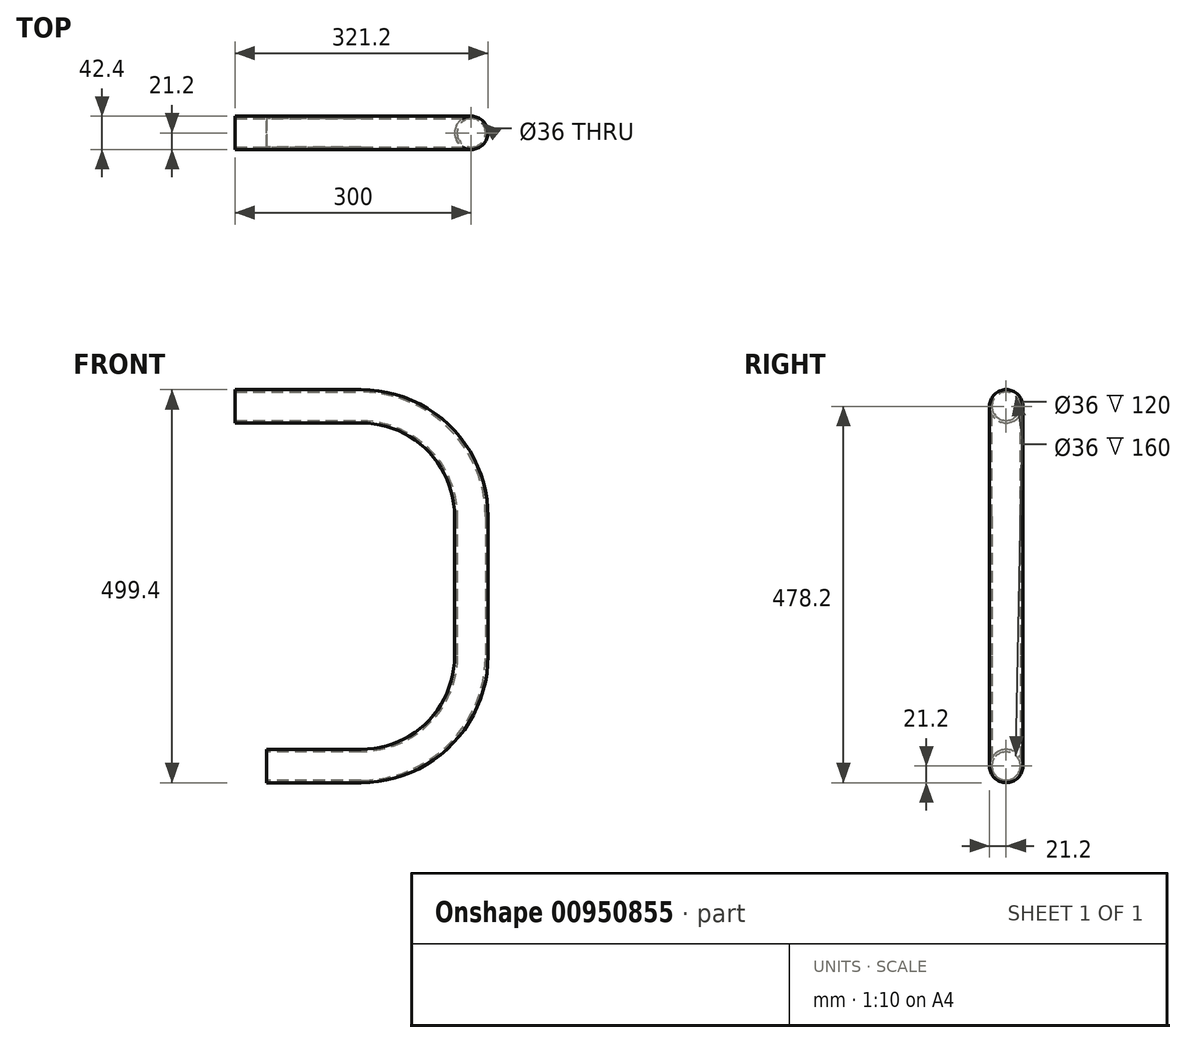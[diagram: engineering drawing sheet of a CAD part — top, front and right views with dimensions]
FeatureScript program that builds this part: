
annotation { "Feature Type Name" : "Feature", "Feature Type Description" : "" }
export const myFeature = defineFeature(function(context is Context, id is Id, definition is map)
    precondition{}
    {
        {
            var Q0;
            Q0=qCreatedBy(makeId("Front.planeOp"),FACE);
            var sketch = newSketch(context, id + "F0", { "sketchPlane" : qUnion([Q0])});
            skLineSegment(sketch, "E0", {"start": v(0, 0) * mm, "end": v(160, 0) * mm});
            skLineSegment(sketch, "E1", {"start": v(300, -140) * mm, "end": v(300, -317) * mm});
            skLineSegment(sketch, "E2", {"start": v(160, -457) * mm, "end": v(40, -457) * mm});
            skPoint(sketch, "E3.visualSharp", {"position": v(300, 0) * mm});
            skArc(sketch, "E3.filletArc", {"start": v(300, -140) * mm, "mid": v(259, -41) * mm, "end": v(160, 0) * mm});
            skPoint(sketch, "E4.visualSharp", {"position": v(300, -457) * mm});
            skArc(sketch, "E4.filletArc", {"start": v(160, -457) * mm, "mid": v(259, -416) * mm, "end": v(300, -317) * mm});
            skSolve(sketch);
        }
        {
            var Q0;
            Q0=qCreatedBy(makeId("Right.planeOp"),FACE);
            var sketch = newSketch(context, id + "F1", { "sketchPlane" : qUnion([Q0])});
            skCircle(sketch, "E5", {"center": v(0, 0) * mm, "radius": 21.2 * mm});
            skCircle(sketch, "E6", {"center": v(0, 0) * mm, "radius": 18 * mm});
            skSolve(sketch);
        }
        {
            var Q0;
            Q0=makeQuery(id+"F1.imprint","IMPRINT",FACE,{"disambiguationData":[TD([[makeQuery(id+"F1.imprint","IMPRINT",EDGE,{"derivedFrom":sQuery(id+"F1.wireOp",EDGE,"E5")}),1.0]])]});
            var Q1;
            Q1=sQuery(id+"F0.wireOp",EDGE,"E0");
            var Q2;
            Q2=sQuery(id+"F0.wireOp",EDGE,"E3.filletArc");
            var Q3;
            Q3=sQuery(id+"F0.wireOp",EDGE,"E1");
            var Q4;
            Q4=sQuery(id+"F0.wireOp",EDGE,"E4.filletArc");
            var Q5;
            Q5=sQuery(id+"F0.wireOp",EDGE,"E2");
            sweep(context, id + "F2", {"profiles" : qUnion([Q0]), "path" : qUnion([Q1, Q2, Q3, Q4, Q5])});
        }
    });
